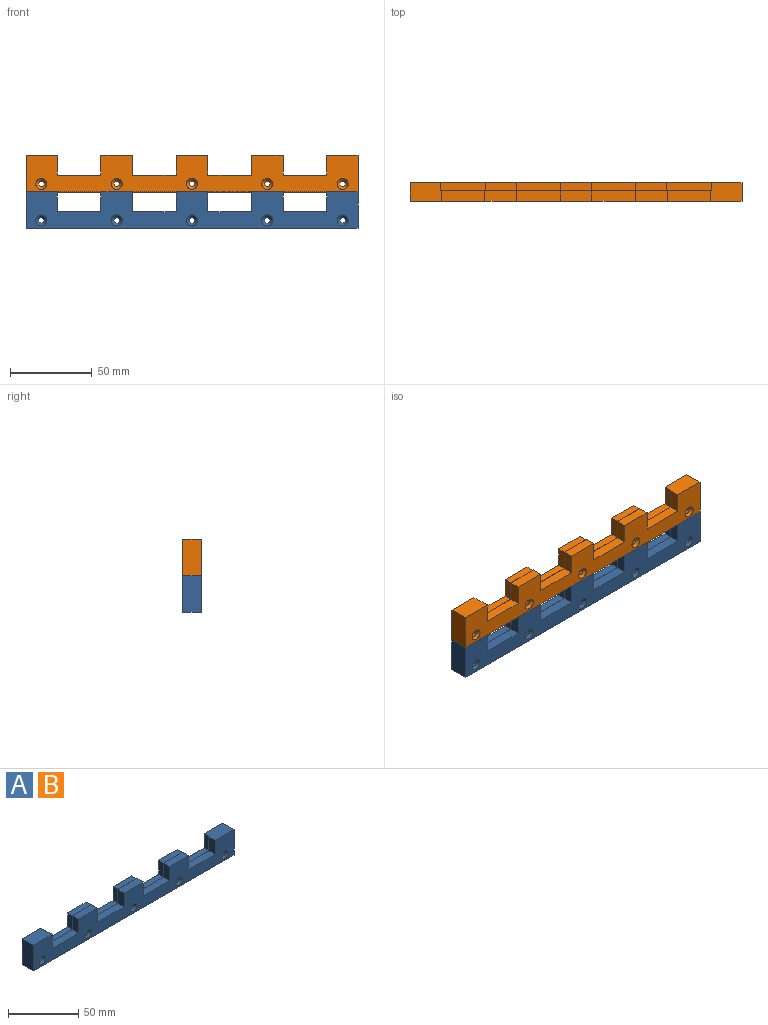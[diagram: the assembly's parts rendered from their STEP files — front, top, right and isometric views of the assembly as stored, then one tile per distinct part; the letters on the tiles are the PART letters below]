
ASSEMBLY  parts=2 mates=1
PART A: 57 faces, bbox 202.6x11.4x22.6 mm
  f0: plane 165.15x12.45mm, normal (0,1,0), area 69.2mm2, adj f5,f6,f7,f8,f9,f10,f11,f12
  f1: plane 165.15x5.08mm, normal (0,0,-1), area 839mm2, adj f2,f25,f27,f28
  f2: plane 5.08x0.25mm, normal (1,0,0), area 1.3mm2, adj f1,f3,f27,f28
  f3: plane 202.64x11.43mm, normal (0,0,-1), area 1477.2mm2, adj f2,f4,f20,f25,f27,f28,f46
  f4: plane 22.35x11.43mm, normal (1,0,0), area 255.5mm2, adj f3,f27,f29,f46
  f5: plane 12.45x5.08mm, normal (-1,0,0), area 63.2mm2, adj f0,f6,f27,f29
  f6: plane 27.23x5.08mm, normal (0,0,1), area 138.3mm2, adj f0,f5,f7,f27
  f7: plane 12.19x5.08mm, normal (1,0,0), area 61.9mm2, adj f0,f6,f8,f27
  f8: plane 18.75x5.08mm, normal (0,0,1), area 95.2mm2, adj f0,f7,f9,f27
  f9: plane 12.19x5.08mm, normal (-1,0,0), area 61.9mm2, adj f0,f8,f10,f27
  f10: plane 27.23x5.08mm, normal (0,0,1), area 138.3mm2, adj f0,f9,f11,f27
  f11: plane 12.19x5.08mm, normal (1,0,0), area 61.9mm2, adj f0,f10,f12,f27
  f12: plane 18.75x5.08mm, normal (0,0,1), area 95.2mm2, adj f0,f11,f13,f27
  f13: plane 12.19x5.08mm, normal (-1,0,0), area 61.9mm2, adj f0,f12,f14,f27
  f14: plane 27.23x5.08mm, normal (0,0,1), area 138.3mm2, adj f0,f13,f15,f27
  f15: plane 12.19x5.08mm, normal (1,0,0), area 61.9mm2, adj f0,f14,f16,f27
  f16: plane 18.75x5.08mm, normal (0,0,1), area 95.2mm2, adj f0,f15,f17,f27
  f17: plane 12.19x5.08mm, normal (-1,0,0), area 61.9mm2, adj f0,f16,f18,f27
  f18: plane 27.23x5.08mm, normal (0,0,1), area 138.3mm2, adj f0,f17,f19,f27
  f19: plane 12.45x5.08mm, normal (1,0,0), area 63.2mm2, adj f0,f18,f27,f45
  f20: plane 22.35x11.43mm, normal (-1,0,0), area 255.5mm2, adj f3,f27,f45,f46
  f21: cylinder r=1.73mm len=8.13mm, axis (0,-1,0), area 88.2mm2, adj f51,f52
  f22: cylinder r=1.73mm len=8.13mm, axis (0,-1,0), area 88.2mm2, adj f53,f54
  f23: cylinder r=1.73mm len=8.13mm, axis (0,-1,0), area 88.2mm2, adj f55,f56
  f24: cylinder r=1.73mm len=8.13mm, axis (0,-1,0), area 88.2mm2, adj f47,f48
  f25: plane 5.08x0.25mm, normal (-1,0,0), area 1.3mm2, adj f1,f3,f27,f28
  f26: cylinder r=1.73mm len=8.13mm, axis (0,-1,0), area 88.2mm2, adj f49,f50
  f27: plane 202.64x22.61mm, normal (0,1,0), area 3022.3mm2, adj f1,f2,f3,f4,f5,f6,f7,f8
  f28: plane 165.15x0.25mm, normal (0,-1,0), area 41.9mm2, adj f1,f2,f3,f25
  f29: plane 19.02x11.43mm, normal (0,0,1), area 216mm2, adj f0,f4,f5,f27,f30,f46
  f30: plane 12.19x6.35mm, normal (-1,0,0), area 77.4mm2, adj f0,f29,f31,f46
  f31: plane 26.67x6.35mm, normal (0,0,1), area 169.4mm2, adj f0,f30,f32,f46
  f32: plane 12.19x6.35mm, normal (1,0,0), area 77.4mm2, adj f0,f31,f33,f46
  f33: plane 19.3x6.35mm, normal (0,0,1), area 122.6mm2, adj f0,f32,f34,f46
  f34: plane 12.19x6.35mm, normal (-1,0,0), area 77.4mm2, adj f0,f33,f35,f46
  f35: plane 26.67x6.35mm, normal (0,0,1), area 169.4mm2, adj f0,f34,f36,f46
  f36: plane 12.19x6.35mm, normal (1,0,0), area 77.4mm2, adj f0,f35,f37,f46
  f37: plane 19.3x6.35mm, normal (0,0,1), area 122.6mm2, adj f0,f36,f38,f46
  f38: plane 12.19x6.35mm, normal (-1,0,0), area 77.4mm2, adj f0,f37,f39,f46
  f39: plane 26.67x6.35mm, normal (0,0,1), area 169.4mm2, adj f0,f38,f40,f46
  f40: plane 12.19x6.35mm, normal (1,0,0), area 77.4mm2, adj f0,f39,f41,f46
  f41: plane 19.3x6.35mm, normal (0,0,1), area 122.6mm2, adj f0,f40,f42,f46
  f42: plane 12.19x6.35mm, normal (-1,0,0), area 77.4mm2, adj f0,f41,f43,f46
  f43: plane 26.67x6.35mm, normal (0,0,1), area 169.4mm2, adj f0,f42,f44,f46
  f44: plane 12.19x6.35mm, normal (1,0,0), area 77.4mm2, adj f0,f43,f45,f46
  f45: plane 19.02x11.43mm, normal (0,0,1), area 216mm2, adj f0,f19,f20,f27,f44,f46
  f46: plane 202.64x22.35mm, normal (0,-1,0), area 3049.5mm2, adj f3,f4,f20,f29,f30,f31,f32,f33
  f47: cone r=1.73mm half-angle=45deg, axis (0,-1,0), area 37.4mm2, adj f24,f46
  f48: cone r=3.38mm half-angle=45deg, axis (0,1,0), area 37.4mm2, adj f24,f27
  f49: cone r=1.73mm half-angle=45deg, axis (0,-1,0), area 37.4mm2, adj f26,f46
  f50: cone r=3.38mm half-angle=45deg, axis (0,1,0), area 37.4mm2, adj f26,f27
  f51: cone r=1.73mm half-angle=45deg, axis (0,-1,0), area 37.4mm2, adj f21,f46
  f52: cone r=3.38mm half-angle=45deg, axis (0,1,0), area 37.4mm2, adj f21,f27
  f53: cone r=1.73mm half-angle=45deg, axis (0,-1,0), area 37.4mm2, adj f22,f46
  f54: cone r=3.38mm half-angle=45deg, axis (0,1,0), area 37.4mm2, adj f22,f27
  f55: cone r=1.73mm half-angle=45deg, axis (0,-1,0), area 37.4mm2, adj f23,f46
  f56: cone r=3.38mm half-angle=45deg, axis (0,1,0), area 37.4mm2, adj f23,f27
PART B: same geometry as A
PLACE A t=(0,0,-22.35)mm
PLACE B at identity
MATE fastened A.f0 <-> B.f28  axis (0,1,0) through (101.32,0,0.25)mm
